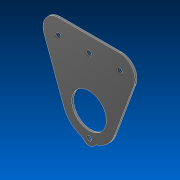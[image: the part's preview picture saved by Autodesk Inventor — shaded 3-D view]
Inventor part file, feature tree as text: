
AUTODESK INVENTOR PART (.ipt)
format: ipt  version: 2022.2 (Build 262287000, 287)  size: 126,976 bytes
history: native  units: in
note: dims shown in document units (in); Inventor stores cm internally (conversion verified against a paired STEP export)
features: extrude x1, sketch x1
ambient origin geometry x8: Origin, YZ Plane, XZ Plane, XY Plane, X Axis, Y Axis, Z Axis, Center Point
bodies: Solid1 (feature_tree)
feature tree (2):
  extrude  "Extrusion1"  Depth=1.625in
  sketch  "Sketch1"  dims[d0=1.0in d4=0.163in d5=1.125in d6=1.75in d7=1.0in d8=0.0625in d9=0.0in d10=0.25in d11=1.3in d12=0.315in d13=1.625in]
